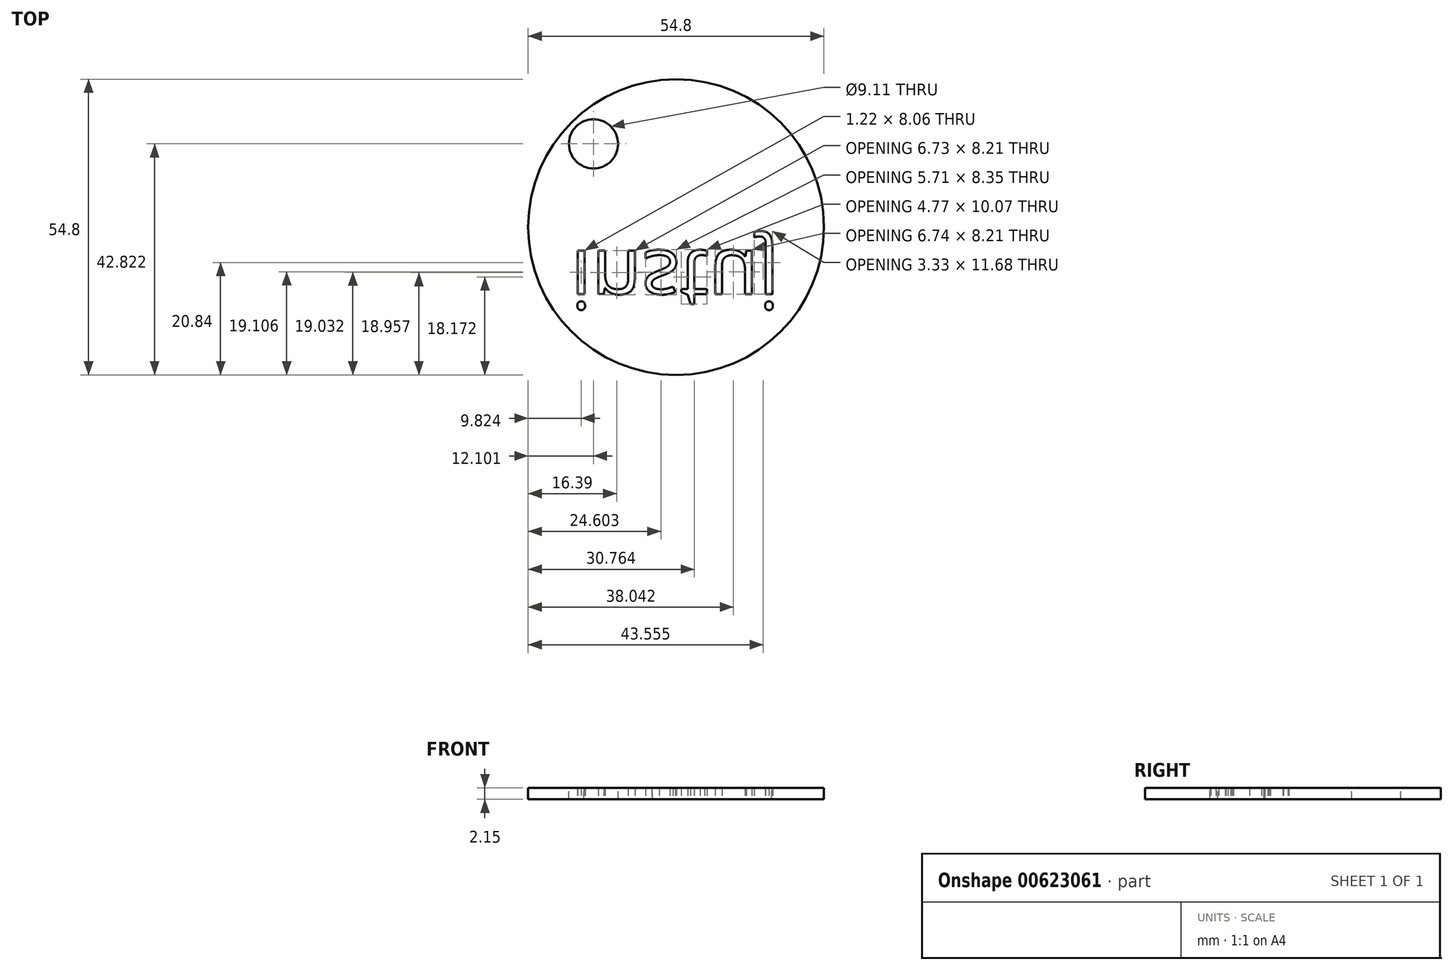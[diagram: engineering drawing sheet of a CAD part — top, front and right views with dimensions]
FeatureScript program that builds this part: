
annotation { "Feature Type Name" : "Feature", "Feature Type Description" : "" }
export const myFeature = defineFeature(function(context is Context, id is Id, definition is map)
    precondition{}
    {
        {
            var Q0;
            Q0=qCreatedBy(makeId("Top.planeOp"),FACE);
            var sketch = newSketch(context, id + "F0", { "sketchPlane" : qUnion([Q0])});
            skCircle(sketch, "E0", {"center": v(0, 0) * mm, "radius": 27.4 * mm});
            skSolve(sketch);
        }
        {
            var Q0;
            Q0=makeQuery(id+"F0.imprint","IMPRINT",FACE,{"disambiguationData":[TD([[makeQuery(id+"F0.imprint","IMPRINT",EDGE,{"derivedFrom":sQuery(id+"F0.wireOp",EDGE,"E0")}),1.0]])]});
            extrude(context, id + "F1", {"entities" : qUnion([Q0]), "depth" : 2.15 * mm, "offsetDistance" : 25 * mm});
        }
        {
            var Q0;
            Q0=makeQuery(id+"F1.opExtrude","CAP_FACE",FACE,{"disambiguationData":[OSD([sQuery(id+"F0.wireOp",EDGE,"E0")])],"isStart":true});
            var sketch = newSketch(context, id + "F2", { "sketchPlane" : qUnion([Q0])});
            skSolve(sketch);
        }
        {
            var Q0;
            Q0=makeQuery(id+"F1.opExtrude","CAP_FACE",FACE,{"disambiguationData":[OSD([sQuery(id+"F0.wireOp",EDGE,"E0")])],"isStart":false});
            var sketch = newSketch(context, id + "F3", { "sketchPlane" : qUnion([Q0])});
            skSolve(sketch);
        }
        {
            var Q0;
            Q0=makeQuery(id+"F3.imprint","IMPRINT",FACE,{"disambiguationData":[TD([[makeQuery(id+"F3.imprint","IMPRINT",EDGE,{"derivedFrom":makeQuery(id+"F1.opExtrude","CAP_EDGE",EDGE,{"disambiguationData":[OSD([sQuery(id+"F0.wireOp",EDGE,"E0")])],"isStart":false})}),1.0]])]});
            var sketch = newSketch(context, id + "F4", { "sketchPlane" : qUnion([Q0])});
            skCircle(sketch, "E1", {"center": v(-15.3, 15.42) * mm, "radius": 4.56 * mm});
            skSolve(sketch);
        }
        {
            var Q0;
            Q0=makeQuery(id+"F4.imprint","IMPRINT",FACE,{"disambiguationData":[TD([[makeQuery(id+"F4.imprint","IMPRINT",EDGE,{"derivedFrom":sQuery(id+"F4.wireOp",EDGE,"E1")}),1.0]])]});
            extrude(context, id + "F5", {"entities" : qUnion([Q0]), "operationType" : NewBodyOperationType.REMOVE, "endBound" : BoundingType.UP_TO_NEXT, "oppositeDirection" : true, "depth" : 25 * mm, "offsetDistance" : 25 * mm});
        }
        {
            var Q0;
            Q0=makeQuery(id+"F2.imprint","IMPRINT",FACE,{"disambiguationData":[TD([[makeQuery(id+"F2.imprint","IMPRINT",EDGE,{"derivedFrom":makeQuery(id+"F1.opExtrude","CAP_EDGE",EDGE,{"disambiguationData":[OSD([sQuery(id+"F0.wireOp",EDGE,"E0")])],"isStart":true})}),-1.0]])]});
            var sketch = newSketch(context, id + "F6", { "sketchPlane" : qUnion([Q0])});
            skText(sketch, "E2", { "text": "instuj", "fontName": "OpenSans-Regular.ttf"});
            const initialGuessF6  = {"E2": [-0.01948, 0.00434, 1, 0, 0.01084]};
            skSetInitialGuess(sketch, initialGuessF6);
            skSolve(sketch);
        }
        {
            var Q0;
            Q0 = qSketchRegion(id + "F6", true);
            extrude(context, id + "F7", {"entities" : qUnion([Q0]), "operationType" : NewBodyOperationType.REMOVE, "endBound" : BoundingType.UP_TO_NEXT, "oppositeDirection" : true, "depth" : 25 * mm, "offsetDistance" : 25 * mm});
        }
    });
